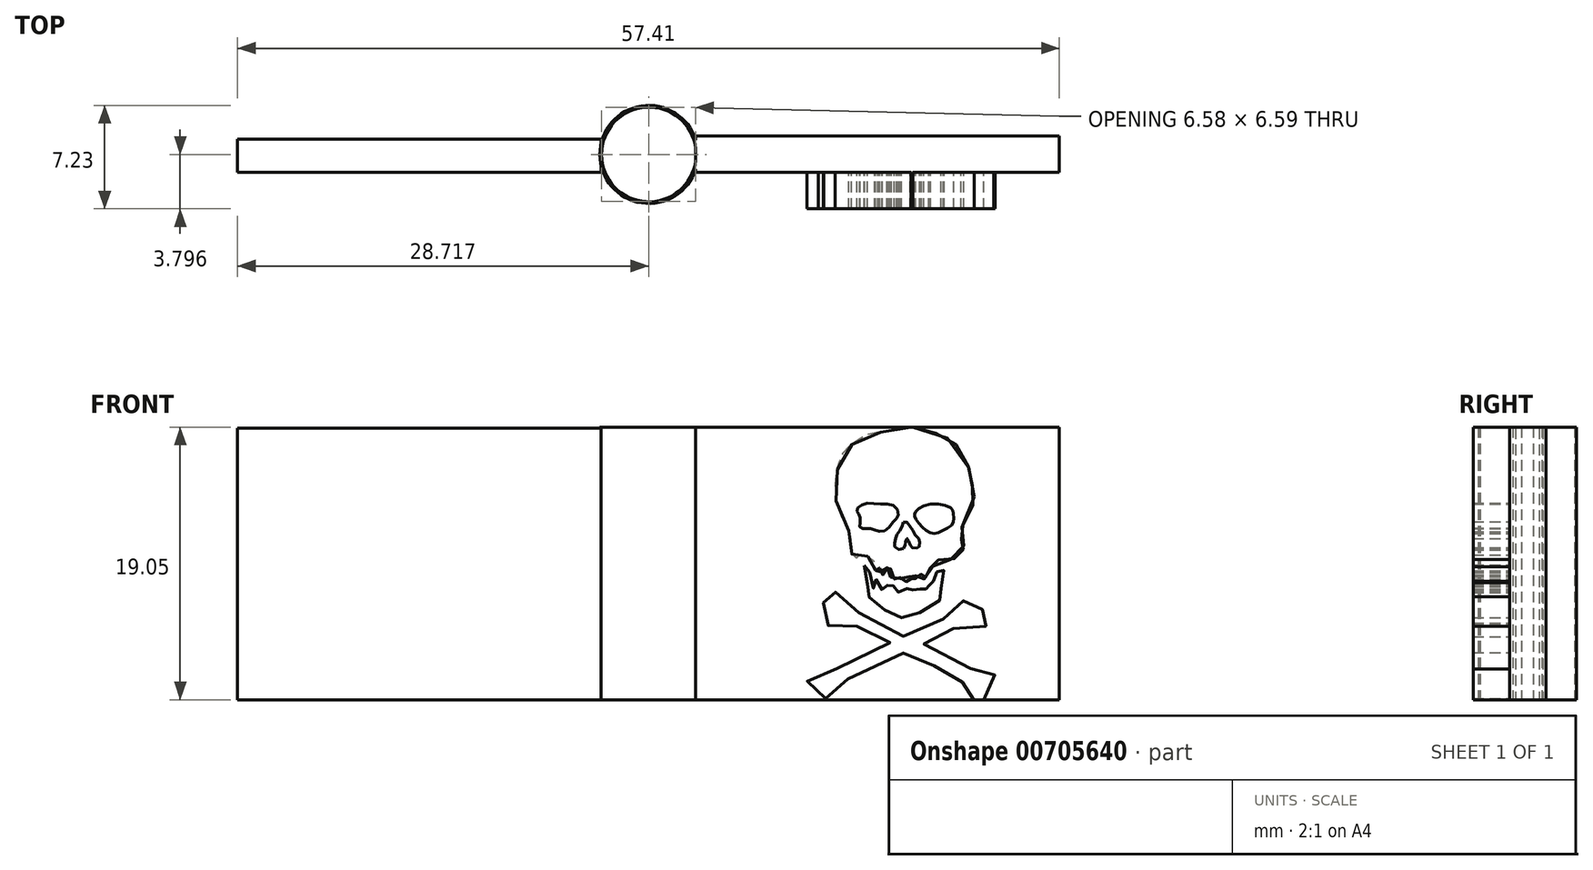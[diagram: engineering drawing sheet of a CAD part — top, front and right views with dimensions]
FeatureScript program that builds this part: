
annotation { "Feature Type Name" : "Feature", "Feature Type Description" : "" }
export const myFeature = defineFeature(function(context is Context, id is Id, definition is map)
    precondition{}
    {
        {
            var Q0;
            Q0=qCreatedBy(makeId("Top.planeOp"),FACE);
            var sketch = newSketch(context, id + "F0", { "sketchPlane" : qUnion([Q0])});
            skCircle(sketch, "E0", {"center": v(0, 1.26) * mm, "radius": 3.43 * mm});
            skSolve(sketch);
        }
        {
            var Q0;
            Q0=makeQuery(id+"F0.imprint","IMPRINT",FACE,{"disambiguationData":[TD([[makeQuery(id+"F0.imprint","IMPRINT",EDGE,{"derivedFrom":sQuery(id+"F0.wireOp",EDGE,"E0")}),1.0]])]});
            extrude(context, id + "F1", {"entities" : qUnion([Q0]), "depth" : 19.05 * mm, "offsetDistance" : 25.4 * mm});
        }
        {
            var Q0;
            Q0=makeQuery(id+"F1.opExtrude","CAP_FACE",FACE,{"disambiguationData":[OSD([sQuery(id+"F0.wireOp",EDGE,"E0")])],"isStart":true});
            var sketch = newSketch(context, id + "F2", { "sketchPlane" : qUnion([Q0])});
            skCircle(sketch, "E1", {"center": v(0, -1.26) * mm, "radius": 3.3 * mm});
            skSolve(sketch);
        }
        {
            var Q0;
            Q0 = qSketchRegion(id + "F2", true);
            extrude(context, id + "F3", {"entities" : qUnion([Q0]), "operationType" : NewBodyOperationType.REMOVE, "oppositeDirection" : true, "depth" : 25.4 * mm, "offsetDistance" : 25.4 * mm});
        }
        {
            var Q0;
            Q0=qCreatedBy(makeId("Right.planeOp"),FACE);
            cPlane(context, id + "F4", {"entities" : qUnion([Q0]), "cplaneType" : CPlaneType.OFFSET, "offset" : 3.28 * mm, "width" : 152.4 * mm, "height" : 152.4 * mm});
        }
        {
            var Q0;
            Q0=qCreatedBy(id+"F4.planeOp",FACE);
            var sketch = newSketch(context, id + "F5", { "sketchPlane" : qUnion([Q0])});
            skLineSegment(sketch, "E2.bottom", {"start": v(0, 0) * mm, "end": v(2.54, 0) * mm});
            skLineSegment(sketch, "E2.top", {"start": v(0, 19.05) * mm, "end": v(2.54, 19.05) * mm});
            skLineSegment(sketch, "E2.left", {"start": v(0, 0) * mm, "end": v(0, 19.05) * mm});
            skLineSegment(sketch, "E2.right", {"start": v(2.54, 0) * mm, "end": v(2.54, 19.05) * mm});
            skSolve(sketch);
        }
        {
            var Q0;
            Q0 = qSketchRegion(id + "F5", true);
            extrude(context, id + "F6", {"entities" : qUnion([Q0]), "operationType" : NewBodyOperationType.ADD, "depth" : 25.4 * mm, "offsetDistance" : 25.4 * mm});
        }
        {
            var Q0;
            Q0=makeQuery(id+"F6.opExtrude","SWEPT_FACE",FACE,{"disambiguationData":[OSD([sQuery(id+"F5.wireOp",EDGE,"E2.left")])]});
            var sketch = newSketch(context, id + "F7", { "sketchPlane" : qUnion([Q0])});
            skFitSpline(sketch, "E3", {"points": [v(16.92, 3.87) * mm, v(12.38, 1.93) * mm, v(11.36, 1.6) * mm, v(11.05, 1.4) * mm, v(11.55, 0.6) * mm, v(11.8, 0.2) * mm, v(12.62, 0.17) * mm, v(13.24, 1.1) * mm, v(14.14, 1.54) * mm, v(17.88, 3.27) * mm, v(18.8, 2.8) * mm, v(20.02, 2.33) * mm, v(21.13, 1.67) * mm, v(21.92, 1.2) * mm, v(22.22, 0.99) * mm, v(22.37, 0.34) * mm, v(22.7, 0) * mm, v(23.38, 0) * mm, v(23.79, 0.99) * mm, v(24.2, 1.5) * mm, v(23.87, 2.05) * mm, v(23.19, 2.12) * mm, v(22.35, 2.23) * mm, v(19.19, 3.83) * mm, v(19.6, 3.96) * mm, v(20.53, 4.5) * mm, v(22.22, 5.3) * mm, v(23.14, 5.16) * mm, v(23.9, 5.33) * mm, v(24, 6.1) * mm, v(23.25, 6.33) * mm, v(22.89, 7) * mm, v(22.1, 7.1) * mm, v(21.88, 6.57) * mm, v(21.52, 6.08) * mm, v(20.13, 5.43) * mm, v(17.99, 4.4) * mm, v(17.22, 4.77) * mm, v(14.18, 6.38) * mm, v(13.56, 7.04) * mm, v(13.05, 7.5) * mm, v(12.53, 7.6) * mm, v(12.2, 7.3) * mm, v(12.21, 6.8) * mm, v(11.87, 6.23) * mm, v(12.15, 5.33) * mm, v(13.09, 5.22) * mm, v(13.75, 5.35) * mm, v(14.95, 4.94) * mm, v(16.32, 4.17) * mm, v(16.92, 3.87) * mm]});
            skFitSpline(sketch, "E4", {"points": [v(15.05, 9.39) * mm, v(15.2, 8.6) * mm, v(15.22, 7.92) * mm, v(15.07, 7.59) * mm, v(15.47, 7.08) * mm, v(16.13, 6.46) * mm, v(16.87, 6.08) * mm, v(17.52, 5.76) * mm, v(18.2, 5.77) * mm, v(19.01, 6.14) * mm, v(20.04, 6.73) * mm, v(20.57, 7.29) * mm, v(20.48, 7.56) * mm, v(20.4, 7.9) * mm, v(20.47, 8.69) * mm, v(20.62, 9.25) * mm, v(20.44, 9.3) * mm, v(20.16, 9.02) * mm, v(19.99, 8.2) * mm, v(19.92, 8.18) * mm, v(19.9, 8.24) * mm, v(19.83, 8.26) * mm, v(19.73, 8.25) * mm, v(19.66, 8.24) * mm, v(19.6, 8.2) * mm, v(19.55, 8.1) * mm, v(19.64, 7.88) * mm, v(19.68, 7.78) * mm, v(19.43, 7.55) * mm, v(19.25, 8) * mm, v(19.02, 7.9) * mm, v(19.06, 7.76) * mm, v(18.89, 7.74) * mm, v(18.72, 7.89) * mm, v(18.54, 7.9) * mm, v(18.42, 7.65) * mm, v(18.33, 7.5) * mm, v(18.13, 7.5) * mm, v(18.06, 7.73) * mm, v(17.66, 7.88) * mm, v(17.64, 7.57) * mm, v(17.32, 7.55) * mm, v(17.3, 7.65) * mm, v(17.23, 7.87) * mm, v(17.15, 7.94) * mm, v(16.92, 7.95) * mm, v(16.9, 7.78) * mm, v(16.75, 7.76) * mm, v(16.57, 8.15) * mm, v(16.28, 8.12) * mm, v(16.3, 7.72) * mm, v(16.03, 7.75) * mm, v(16.02, 8.32) * mm, v(15.8, 8.34) * mm, v(15.83, 7.76) * mm, v(15.77, 7.7) * mm, v(15.63, 7.91) * mm, v(15.45, 8.6) * mm, v(15.4, 9.02) * mm, v(15.3, 9.3) * mm, v(15.16, 9.4) * mm, v(15.05, 9.39) * mm]});
            skFitSpline(sketch, "E5", {"points": [v(13, 14.84) * mm, v(13.22, 13.37) * mm, v(13.83, 12.03) * mm, v(14.14, 11.26) * mm, v(13.98, 10.56) * mm, v(14.53, 9.88) * mm, v(14.62, 10.06) * mm, v(15.16, 10.06) * mm, v(15.72, 9.68) * mm, v(15.8, 9.25) * mm, v(15.8, 9.07) * mm, v(15.93, 9.03) * mm, v(15.97, 9.25) * mm, v(16.11, 9.25) * mm, v(16.1, 9.13) * mm, v(16.13, 8.96) * mm, v(16.28, 8.75) * mm, v(16.57, 8.74) * mm, v(16.7, 9.07) * mm, v(16.65, 9.32) * mm, v(16.91, 9.35) * mm, v(16.87, 9.05) * mm, v(16.94, 8.49) * mm, v(17.22, 8.46) * mm, v(17.31, 8.62) * mm, v(17.54, 8.6) * mm, v(17.58, 8.35) * mm, v(17.81, 8.24) * mm, v(17.95, 8.24) * mm, v(18.06, 8.54) * mm, v(18.27, 8.53) * mm, v(18.27, 8.24) * mm, v(18.61, 8.24) * mm, v(18.64, 8.75) * mm, v(18.98, 8.87) * mm, v(19.01, 8.69) * mm, v(19.14, 8.49) * mm, v(19.29, 8.46) * mm, v(19.36, 9.1) * mm, v(19.47, 9.14) * mm, v(19.9, 9.35) * mm, v(20.16, 9.73) * mm, v(20.62, 9.78) * mm, v(21.59, 9.94) * mm, v(21.9, 10.35) * mm, v(22, 10.74) * mm, v(21.92, 10.96) * mm, v(21.8, 11.6) * mm, v(21.94, 12.2) * mm, v(22.67, 13.68) * mm, v(22.62, 14.83) * mm, v(22.4, 16) * mm, v(21.54, 17.77) * mm, v(20, 18.64) * mm, v(18.3, 19.05) * mm, v(17.15, 18.78) * mm, v(15.67, 18.64) * mm, v(14.49, 18.06) * mm, v(13.56, 17.23) * mm, v(13.16, 16.08) * mm, v(13, 14.84) * mm]});
            skFitSpline(sketch, "E6", {"points": [v(14.6, 13.4) * mm, v(14.55, 13.15) * mm, v(14.7, 12.88) * mm, v(14.76, 12.42) * mm, v(14.77, 12) * mm, v(15.15, 11.95) * mm, v(15.5, 11.97) * mm, v(15.94, 11.79) * mm, v(16.57, 11.85) * mm, v(17.15, 12.53) * mm, v(17.43, 12.86) * mm, v(17.15, 13.53) * mm, v(16.2, 13.67) * mm, v(15.18, 13.7) * mm, v(14.6, 13.4) * mm]});
            skFitSpline(sketch, "E7", {"points": [v(17.78, 12.4) * mm, v(17.7, 12.1) * mm, v(17.57, 11.87) * mm, v(17.4, 11.66) * mm, v(17.29, 11.44) * mm, v(17.22, 11.15) * mm, v(17.15, 10.9) * mm, v(17.15, 10.73) * mm, v(17.39, 10.52) * mm, v(17.67, 10.5) * mm, v(17.87, 10.66) * mm, v(17.92, 10.82) * mm, v(17.94, 11.04) * mm, v(17.97, 11.2) * mm, v(18.06, 11.26) * mm, v(18.14, 11.1) * mm, v(18.18, 10.93) * mm, v(18.29, 10.74) * mm, v(18.4, 10.61) * mm, v(18.7, 10.6) * mm, v(18.81, 10.59) * mm, v(18.91, 10.8) * mm, v(18.91, 11.01) * mm, v(18.88, 11.22) * mm, v(18.64, 11.44) * mm, v(18.5, 11.68) * mm, v(18.28, 12.06) * mm, v(18.08, 12.32) * mm, v(18, 12.42) * mm, v(17.78, 12.4) * mm]});
            skFitSpline(sketch, "E8", {"points": [v(18.63, 13.14) * mm, v(19.66, 13.66) * mm, v(21.16, 13.34) * mm, v(21.25, 12.96) * mm, v(21.25, 12.32) * mm, v(20.62, 11.86) * mm, v(19.87, 11.61) * mm, v(19.22, 11.94) * mm, v(18.64, 12.64) * mm, v(18.55, 12.93) * mm, v(18.63, 13.14) * mm]});
            skSolve(sketch);
        }
        {
            var Q0;
            Q0=makeQuery(id+"F7.imprint","IMPRINT",FACE,{"disambiguationData":[TD([[makeQuery(id+"F7.imprint","IMPRINT",EDGE,{"derivedFrom":sQuery(id+"F7.wireOp",EDGE,"E6")}),-1.0]])]});
            var Q1;
            Q1=makeQuery(id+"F7.imprint","IMPRINT",FACE,{"disambiguationData":[TD([[makeQuery(id+"F7.imprint","IMPRINT",EDGE,{"derivedFrom":sQuery(id+"F7.wireOp",EDGE,"E4")}),1.0]])]});
            var Q2;
            {var subQ0=sQuery(id+"F7.wireOp",EDGE,"E3");var subQ1=makeQuery(id+"F6.opExtrude","SWEPT_EDGE",EDGE,{"disambiguationData":[OSD([sQuery(id+"F5.wireOp",EDGE,"E2.bottom"),sQuery(id+"F5.wireOp",EDGE,"E2.left")])]});var subQ2=makeQuery(id+"F7.imprint","INTERSECT",VERTEX,{"disambiguationData":[OD(0.0)],"derivedFrom":[subQ1,subQ0]});Q2=makeQuery(id+"F7.imprint","IMPRINT",FACE,{"disambiguationData":[TD([[makeQuery(id+"F7.imprint","IMPRINT",EDGE,{"disambiguationData":[TD([[subQ2,1.0]])],"derivedFrom":subQ0}),1.0]])]});}
            extrude(context, id + "F8", {"entities" : qUnion([Q0, Q1, Q2]), "operationType" : NewBodyOperationType.ADD, "depth" : 2.54 * mm, "offsetDistance" : 25.4 * mm});
        }
        {
            var Q0;
            Q0=qCreatedBy(id+"F4.planeOp",FACE);
            cPlane(context, id + "F9", {"entities" : qUnion([Q0]), "cplaneType" : CPlaneType.OFFSET, "offset" : 6.6 * mm, "oppositeDirection" : true, "width" : 152.4 * mm, "height" : 152.4 * mm});
        }
        {
            var Q0;
            Q0=qCreatedBy(id+"F9.planeOp",FACE);
            var sketch = newSketch(context, id + "F10", { "sketchPlane" : qUnion([Q0])});
            skPoint(sketch, "E9.top.end.orphan", {"position": v(0, 18.6) * mm});
            skLineSegment(sketch, "E10.bottom", {"start": v(2.34, 18.96) * mm, "end": v(0, 18.96) * mm});
            skLineSegment(sketch, "E10.top", {"start": v(2.34, 0) * mm, "end": v(0, 0) * mm});
            skLineSegment(sketch, "E10.left", {"start": v(2.34, 18.96) * mm, "end": v(2.34, 0) * mm});
            skLineSegment(sketch, "E10.right", {"start": v(0, 18.96) * mm, "end": v(0, 0) * mm});
            skSolve(sketch);
        }
        {
            var Q0;
            Q0 = qSketchRegion(id + "F10", true);
            extrude(context, id + "F11", {"entities" : qUnion([Q0]), "operationType" : NewBodyOperationType.ADD, "oppositeDirection" : true, "depth" : 25.4 * mm, "offsetDistance" : 25.4 * mm});
        }
    });
